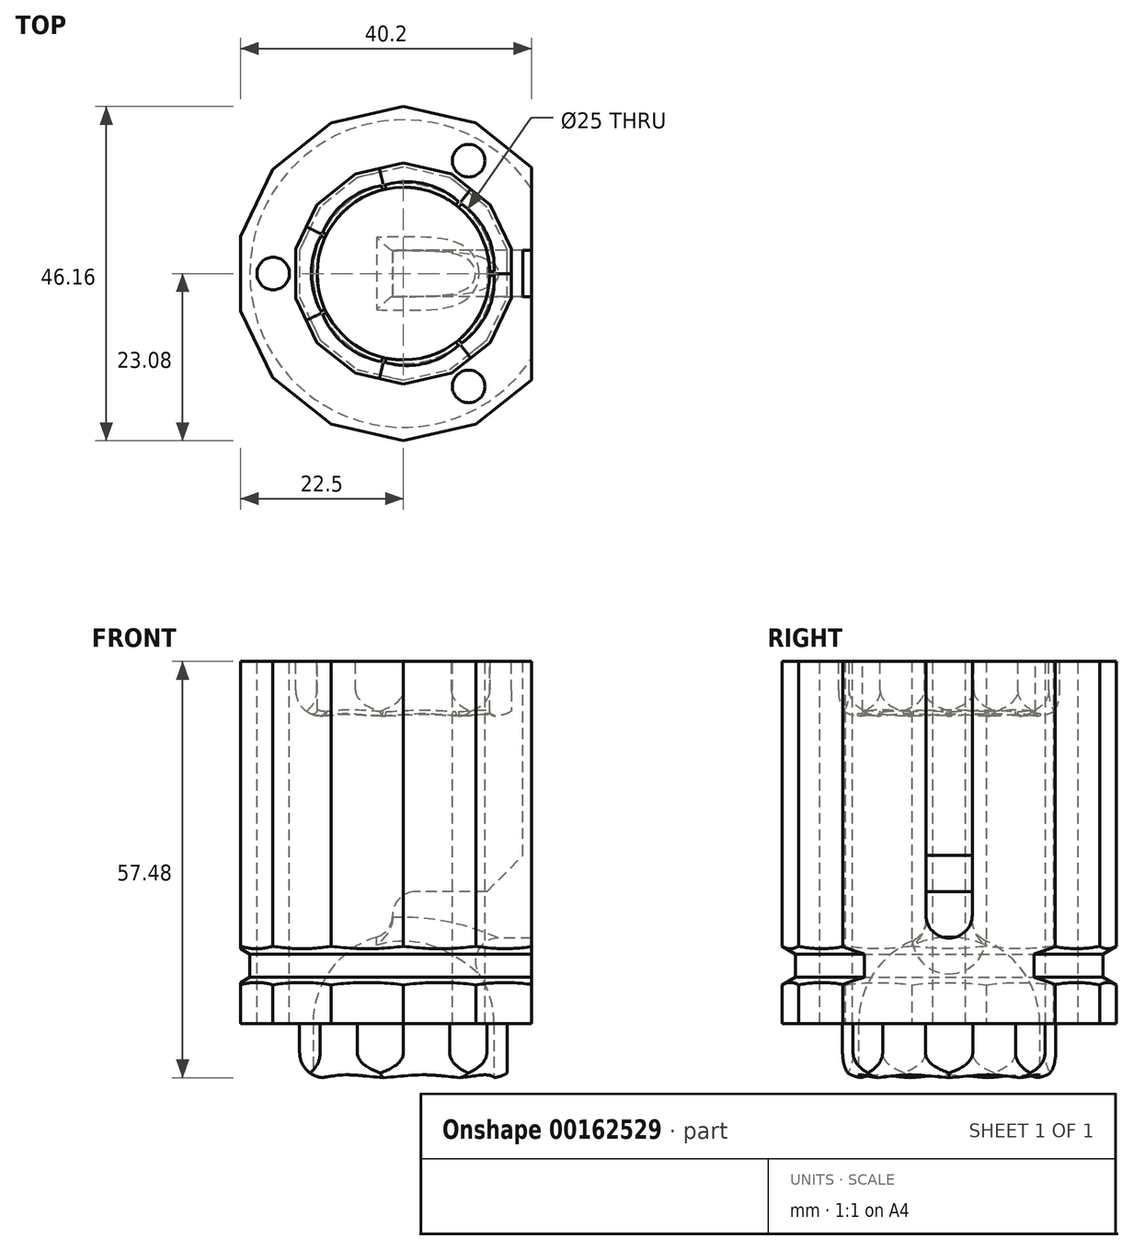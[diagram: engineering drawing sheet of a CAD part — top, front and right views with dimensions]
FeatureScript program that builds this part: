
annotation { "Feature Type Name" : "Feature", "Feature Type Description" : "" }
export const myFeature = defineFeature(function(context is Context, id is Id, definition is map)
    precondition{}
    {
        {
            var Q0;
            Q0=qCreatedBy(makeId("Top.planeOp"),FACE);
            var sketch = newSketch(context, id + "F0", { "sketchPlane" : qUnion([Q0])});
            skCircle(sketch, "E0", {"center": v(0, 0) * mm, "radius": 12.5 * mm});
            skCircle(sketch, "E1.cCircle", {"center": v(0, 0) * mm, "radius": 17.5 * mm, "construction": true});
            skLineSegment(sketch, "E1.0", {"start": v(17.5, 8.43) * mm, "end": v(17.5, -8.43) * mm, "construction": true});
            skLineSegment(sketch, "E1.1", {"start": v(17.5, -8.43) * mm, "end": v(4.32, -18.94) * mm, "construction": true});
            skLineSegment(sketch, "E1.2", {"start": v(4.32, -18.94) * mm, "end": v(-12.11, -15.19) * mm, "construction": true});
            skLineSegment(sketch, "E1.3", {"start": v(-12.11, -15.19) * mm, "end": v(-19.42, 0) * mm, "construction": true});
            skLineSegment(sketch, "E1.4", {"start": v(-19.42, 0) * mm, "end": v(-12.11, 15.19) * mm, "construction": true});
            skLineSegment(sketch, "E1.5", {"start": v(-12.11, 15.19) * mm, "end": v(4.32, 18.94) * mm, "construction": true});
            skLineSegment(sketch, "E1.6", {"start": v(4.32, 18.94) * mm, "end": v(17.5, 8.43) * mm, "construction": true});
            skPoint(sketch, "E1.0.midPoint", {"position": v(17.5, 0) * mm});
            skArc(sketch, "E2", {"start": v(7.16, 16.67) * mm, "mid": v(13.9, 17.43) * mm, "end": v(14.66, 10.69) * mm, "construction": true});
            skArc(sketch, "E3", {"start": v(0.79, 18.13) * mm, "mid": v(-4.96, 21.74) * mm, "end": v(-8.57, 16) * mm, "construction": true});
            skArc(sketch, "E4", {"start": v(-13.68, 11.92) * mm, "mid": v(-20.1, 9.68) * mm, "end": v(-17.85, 3.27) * mm, "construction": true});
            skArc(sketch, "E5", {"start": v(-17.85, -3.27) * mm, "mid": v(-20.1, -9.68) * mm, "end": v(-13.68, -11.92) * mm, "construction": true});
            skArc(sketch, "E6", {"start": v(-8.57, -16) * mm, "mid": v(-4.96, -21.74) * mm, "end": v(0.79, -18.13) * mm, "construction": true});
            skArc(sketch, "E7", {"start": v(14.66, -10.69) * mm, "mid": v(13.9, -17.43) * mm, "end": v(7.16, -16.67) * mm, "construction": true});
            skCircle(sketch, "E8.cCircle", {"center": v(0, 0) * mm, "radius": 22.5 * mm, "construction": true});
            skLineSegment(sketch, "E8.0", {"start": v(22.5, 5.14) * mm, "end": v(22.5, -5.14) * mm});
            skLineSegment(sketch, "E8.1", {"start": v(22.5, -5.14) * mm, "end": v(18.04, -14.39) * mm});
            skLineSegment(sketch, "E8.2", {"start": v(18.04, -14.39) * mm, "end": v(10.01, -20.8) * mm});
            skLineSegment(sketch, "E8.3", {"start": v(10.01, -20.8) * mm, "end": v(0, -23.08) * mm});
            skLineSegment(sketch, "E8.4", {"start": v(0, -23.08) * mm, "end": v(-10.01, -20.8) * mm});
            skLineSegment(sketch, "E8.5", {"start": v(-10.01, -20.8) * mm, "end": v(-18.04, -14.39) * mm});
            skLineSegment(sketch, "E8.6", {"start": v(-18.04, -14.39) * mm, "end": v(-22.5, -5.14) * mm});
            skLineSegment(sketch, "E8.7", {"start": v(-22.5, -5.14) * mm, "end": v(-22.5, 5.14) * mm});
            skLineSegment(sketch, "E8.8", {"start": v(-22.5, 5.14) * mm, "end": v(-18.04, 14.39) * mm});
            skLineSegment(sketch, "E8.9", {"start": v(-18.04, 14.39) * mm, "end": v(-10.01, 20.8) * mm});
            skLineSegment(sketch, "E8.10", {"start": v(-10.01, 20.8) * mm, "end": v(0, 23.08) * mm});
            skLineSegment(sketch, "E8.11", {"start": v(0, 23.08) * mm, "end": v(10.01, 20.8) * mm});
            skLineSegment(sketch, "E8.12", {"start": v(10.01, 20.8) * mm, "end": v(18.04, 14.39) * mm});
            skLineSegment(sketch, "E8.13", {"start": v(18.04, 14.39) * mm, "end": v(22.5, 5.14) * mm});
            skPoint(sketch, "E8.0.midPoint", {"position": v(22.5, 0) * mm});
            skSolve(sketch);
        }
        {
            var Q0;
            Q0=qSketchRegion(id+"F0",true);
            extrude(context, id + "F1", {"entities" : qUnion([Q0]), "endBound" : BoundingType.SYMMETRIC, "depth" : 50 * mm, "offsetDistance" : 25 * mm});
        }
        {
            var Q0;
            Q0=makeQuery(id+"F1.opExtrude","CAP_FACE",FACE,{"disambiguationData":[OSD([sQuery(id+"F0.wireOp",EDGE,"E0"),sQuery(id+"F0.wireOp",EDGE,"E1.0"),sQuery(id+"F0.wireOp",EDGE,"E1.1"),sQuery(id+"F0.wireOp",EDGE,"E1.2"),sQuery(id+"F0.wireOp",EDGE,"E1.3"),sQuery(id+"F0.wireOp",EDGE,"E1.4"),sQuery(id+"F0.wireOp",EDGE,"E1.5"),sQuery(id+"F0.wireOp",EDGE,"E1.6"),sQuery(id+"F0.wireOp",EDGE,"E2"),sQuery(id+"F0.wireOp",EDGE,"E3"),sQuery(id+"F0.wireOp",EDGE,"E4"),sQuery(id+"F0.wireOp",EDGE,"E5"),sQuery(id+"F0.wireOp",EDGE,"E6"),sQuery(id+"F0.wireOp",EDGE,"E7")])],"isStart":false});
            var sketch = newSketch(context, id + "F2", { "sketchPlane" : qUnion([Q0])});
            skLineSegment(sketch, "E9", {"start": v(0, 0) * mm, "end": v(11.38, 19.7) * mm, "construction": true});
            skCircle(sketch, "E10", {"center": v(9, 15.59) * mm, "radius": 2.25 * mm});
            skCircle(sketch, "E11.1.0", {"center": v(-18, 0) * mm, "radius": 2.25 * mm});
            skCircle(sketch, "E11.2.0", {"center": v(9, -15.59) * mm, "radius": 2.25 * mm});
            skPoint(sketch, "E11.center", {"position": v(0, 0) * mm});
            skSolve(sketch);
        }
        {
            var Q0;
            Q0=qSketchRegion(id+"F2",true);
            extrude(context, id + "F3", {"entities" : qUnion([Q0]), "operationType" : NewBodyOperationType.REMOVE, "oppositeDirection" : true, "depth" : 50 * mm, "offsetDistance" : 25 * mm});
        }
        {
            var Q0;
            Q0=makeQuery(id+"F1.opExtrude","CAP_FACE",FACE,{"disambiguationData":[OSD([sQuery(id+"F0.wireOp",EDGE,"E0"),sQuery(id+"F0.wireOp",EDGE,"E1.0"),sQuery(id+"F0.wireOp",EDGE,"E1.1"),sQuery(id+"F0.wireOp",EDGE,"E1.2"),sQuery(id+"F0.wireOp",EDGE,"E1.3"),sQuery(id+"F0.wireOp",EDGE,"E1.4"),sQuery(id+"F0.wireOp",EDGE,"E1.5"),sQuery(id+"F0.wireOp",EDGE,"E1.6"),sQuery(id+"F0.wireOp",EDGE,"E2"),sQuery(id+"F0.wireOp",EDGE,"E3"),sQuery(id+"F0.wireOp",EDGE,"E4"),sQuery(id+"F0.wireOp",EDGE,"E5"),sQuery(id+"F0.wireOp",EDGE,"E6"),sQuery(id+"F0.wireOp",EDGE,"E7")])],"isStart":false});
            var sketch = newSketch(context, id + "F4", { "sketchPlane" : qUnion([Q0])});
            skCircle(sketch, "E12", {"center": v(0, 0) * mm, "radius": 12.5 * mm});
            skCircle(sketch, "E13.cCircle", {"center": v(0, 0) * mm, "radius": 14.9 * mm, "construction": true});
            skLineSegment(sketch, "E13.0", {"start": v(14.9, 3.4) * mm, "end": v(14.9, -3.4) * mm});
            skLineSegment(sketch, "E13.1", {"start": v(14.9, -3.4) * mm, "end": v(11.95, -9.53) * mm});
            skLineSegment(sketch, "E13.2", {"start": v(11.95, -9.53) * mm, "end": v(6.63, -13.77) * mm});
            skLineSegment(sketch, "E13.3", {"start": v(6.63, -13.77) * mm, "end": v(0, -15.28) * mm});
            skLineSegment(sketch, "E13.4", {"start": v(0, -15.28) * mm, "end": v(-6.63, -13.77) * mm});
            skLineSegment(sketch, "E13.5", {"start": v(-6.63, -13.77) * mm, "end": v(-11.95, -9.53) * mm});
            skLineSegment(sketch, "E13.6", {"start": v(-11.95, -9.53) * mm, "end": v(-14.9, -3.4) * mm});
            skLineSegment(sketch, "E13.7", {"start": v(-14.9, -3.4) * mm, "end": v(-14.9, 3.4) * mm});
            skLineSegment(sketch, "E13.8", {"start": v(-14.9, 3.4) * mm, "end": v(-11.95, 9.53) * mm});
            skLineSegment(sketch, "E13.9", {"start": v(-11.95, 9.53) * mm, "end": v(-6.63, 13.77) * mm});
            skLineSegment(sketch, "E13.10", {"start": v(-6.63, 13.77) * mm, "end": v(0, 15.28) * mm});
            skLineSegment(sketch, "E13.11", {"start": v(0, 15.28) * mm, "end": v(6.63, 13.77) * mm});
            skLineSegment(sketch, "E13.12", {"start": v(6.63, 13.77) * mm, "end": v(11.95, 9.53) * mm});
            skLineSegment(sketch, "E13.13", {"start": v(11.95, 9.53) * mm, "end": v(14.9, 3.4) * mm});
            skPoint(sketch, "E13.0.midPoint", {"position": v(14.9, 0) * mm});
            skSolve(sketch);
        }
        {
            var Q0;
            Q0=qSketchRegion(id+"F4",true);
            extrude(context, id + "F5", {"entities" : qUnion([Q0]), "operationType" : NewBodyOperationType.REMOVE, "oppositeDirection" : true, "depth" : 7.5 * mm, "offsetDistance" : 25 * mm});
        }
        {
            var Q0;
            Q0=makeQuery(id+"F5.boolean.opBoolean","COPY",EDGE,{"derivedFrom":makeQuery(id+"F5.opExtrude","CAP_EDGE",EDGE,{"disambiguationData":[OSD([sQuery(id+"F4.wireOp",EDGE,"E13.9")])],"isStart":false})});
            var Q1;
            Q1=makeQuery(id+"F5.boolean.opBoolean","COPY",EDGE,{"derivedFrom":makeQuery(id+"F5.opExtrude","CAP_EDGE",EDGE,{"disambiguationData":[OSD([sQuery(id+"F4.wireOp",EDGE,"E13.11")])],"isStart":false})});
            var Q2;
            Q2=makeQuery(id+"F5.boolean.opBoolean","COPY",EDGE,{"derivedFrom":makeQuery(id+"F5.opExtrude","CAP_EDGE",EDGE,{"disambiguationData":[OSD([sQuery(id+"F4.wireOp",EDGE,"E13.13")])],"isStart":false})});
            var Q3;
            Q3=makeQuery(id+"F5.boolean.opBoolean","COPY",EDGE,{"derivedFrom":makeQuery(id+"F5.opExtrude","CAP_EDGE",EDGE,{"disambiguationData":[OSD([sQuery(id+"F4.wireOp",EDGE,"E13.1")])],"isStart":false})});
            var Q4;
            Q4=makeQuery(id+"F5.boolean.opBoolean","COPY",EDGE,{"derivedFrom":makeQuery(id+"F5.opExtrude","CAP_EDGE",EDGE,{"disambiguationData":[OSD([sQuery(id+"F4.wireOp",EDGE,"E13.3")])],"isStart":false})});
            var Q5;
            Q5=makeQuery(id+"F5.boolean.opBoolean","COPY",EDGE,{"derivedFrom":makeQuery(id+"F5.opExtrude","CAP_EDGE",EDGE,{"disambiguationData":[OSD([sQuery(id+"F4.wireOp",EDGE,"E13.5")])],"isStart":false})});
            var Q6;
            {var subQ0=sQuery(id+"F4.wireOp",EDGE,"E13.8");var subQ1=sQuery(id+"F4.wireOp",EDGE,"E13.7");Q6=makeQuery(id+"F5.boolean.opBoolean","COPY",EDGE,{"disambiguationData":[TD([makeQuery(id+"F5.opExtrude","SWEPT_FACE",FACE,{"disambiguationData":[OSD([subQ0])]})])],"derivedFrom":makeQuery(id+"F5.opExtrude","CAP_EDGE",EDGE,{"disambiguationData":[OSD([subQ1])],"isStart":false})});}
            fillet(context, id + "F6", {"entities" : qUnion([Q0, Q1, Q2, Q3, Q4, Q5, Q6]), "radius" : 3.5 * mm, "tangentPropagation" : true, "allowEdgeOverflow" : false});
        }
        {
            var Q0;
            Q0=makeQuery(id+"F1.opExtrude","CAP_FACE",FACE,{"disambiguationData":[OSD([sQuery(id+"F0.wireOp",EDGE,"E0"),sQuery(id+"F0.wireOp",EDGE,"E1.0"),sQuery(id+"F0.wireOp",EDGE,"E1.1"),sQuery(id+"F0.wireOp",EDGE,"E1.2"),sQuery(id+"F0.wireOp",EDGE,"E1.3"),sQuery(id+"F0.wireOp",EDGE,"E1.4"),sQuery(id+"F0.wireOp",EDGE,"E1.5"),sQuery(id+"F0.wireOp",EDGE,"E1.6"),sQuery(id+"F0.wireOp",EDGE,"E2"),sQuery(id+"F0.wireOp",EDGE,"E3"),sQuery(id+"F0.wireOp",EDGE,"E4"),sQuery(id+"F0.wireOp",EDGE,"E5"),sQuery(id+"F0.wireOp",EDGE,"E6"),sQuery(id+"F0.wireOp",EDGE,"E7")])],"isStart":true});
            var sketch = newSketch(context, id + "F7", { "sketchPlane" : qUnion([Q0])});
            skCircle(sketch, "E14", {"center": v(0, 0) * mm, "radius": 12.5 * mm});
            skCircle(sketch, "E15.cCircle", {"center": v(0, 0) * mm, "radius": 14.35 * mm, "construction": true});
            skLineSegment(sketch, "E15.0", {"start": v(14.35, 3.28) * mm, "end": v(14.35, -3.28) * mm});
            skLineSegment(sketch, "E15.1", {"start": v(14.35, -3.28) * mm, "end": v(11.5, -9.18) * mm});
            skLineSegment(sketch, "E15.2", {"start": v(11.5, -9.18) * mm, "end": v(6.39, -13.26) * mm});
            skLineSegment(sketch, "E15.3", {"start": v(6.39, -13.26) * mm, "end": v(0, -14.72) * mm});
            skLineSegment(sketch, "E15.4", {"start": v(0, -14.72) * mm, "end": v(-6.39, -13.26) * mm});
            skLineSegment(sketch, "E15.5", {"start": v(-6.39, -13.26) * mm, "end": v(-11.5, -9.18) * mm});
            skLineSegment(sketch, "E15.6", {"start": v(-11.5, -9.18) * mm, "end": v(-14.35, -3.28) * mm});
            skLineSegment(sketch, "E15.7", {"start": v(-14.35, -3.28) * mm, "end": v(-14.35, 3.28) * mm});
            skLineSegment(sketch, "E15.8", {"start": v(-14.35, 3.28) * mm, "end": v(-11.5, 9.18) * mm});
            skLineSegment(sketch, "E15.9", {"start": v(-11.5, 9.18) * mm, "end": v(-6.39, 13.26) * mm});
            skLineSegment(sketch, "E15.10", {"start": v(-6.39, 13.26) * mm, "end": v(0, 14.72) * mm});
            skLineSegment(sketch, "E15.11", {"start": v(0, 14.72) * mm, "end": v(6.39, 13.26) * mm});
            skLineSegment(sketch, "E15.12", {"start": v(6.39, 13.26) * mm, "end": v(11.5, 9.18) * mm});
            skLineSegment(sketch, "E15.13", {"start": v(11.5, 9.18) * mm, "end": v(14.35, 3.28) * mm});
            skPoint(sketch, "E15.0.midPoint", {"position": v(14.35, 0) * mm});
            skSolve(sketch);
        }
        {
            var Q0;
            Q0=qSketchRegion(id+"F7",true);
            extrude(context, id + "F8", {"entities" : qUnion([Q0]), "operationType" : NewBodyOperationType.ADD, "depth" : 7.5 * mm, "offsetDistance" : 25 * mm});
        }
        {
            var Q0;
            Q0=makeQuery(id+"F8.opExtrude","CAP_EDGE",EDGE,{"disambiguationData":[OSD([sQuery(id+"F7.wireOp",EDGE,"E15.1")])],"isStart":false});
            var Q1;
            Q1=makeQuery(id+"F8.opExtrude","CAP_EDGE",EDGE,{"disambiguationData":[OSD([sQuery(id+"F7.wireOp",EDGE,"E15.3")])],"isStart":false});
            var Q2;
            Q2=makeQuery(id+"F8.opExtrude","CAP_EDGE",EDGE,{"disambiguationData":[OSD([sQuery(id+"F7.wireOp",EDGE,"E15.5")])],"isStart":false});
            var Q3;
            Q3=makeQuery(id+"F8.opExtrude","CAP_EDGE",EDGE,{"disambiguationData":[OSD([sQuery(id+"F7.wireOp",EDGE,"E15.7")])],"isStart":false});
            var Q4;
            Q4=makeQuery(id+"F8.opExtrude","CAP_EDGE",EDGE,{"disambiguationData":[OSD([sQuery(id+"F7.wireOp",EDGE,"E15.9")])],"isStart":false});
            var Q5;
            Q5=makeQuery(id+"F8.opExtrude","CAP_EDGE",EDGE,{"disambiguationData":[OSD([sQuery(id+"F7.wireOp",EDGE,"E15.11")])],"isStart":false});
            var Q6;
            Q6=makeQuery(id+"F8.opExtrude","CAP_EDGE",EDGE,{"disambiguationData":[OSD([sQuery(id+"F7.wireOp",EDGE,"E15.13")])],"isStart":false});
            fillet(context, id + "F9", {"entities" : qUnion([Q0, Q1, Q2, Q3, Q4, Q5, Q6]), "radius" : 3.5 * mm, "tangentPropagation" : true, "allowEdgeOverflow" : false});
        }
        {
            var Q0;
            Q0=makeQuery(id+"F1.opExtrude","CAP_FACE",FACE,{"disambiguationData":[OSD([sQuery(id+"F0.wireOp",EDGE,"E0"),sQuery(id+"F0.wireOp",EDGE,"E1.0"),sQuery(id+"F0.wireOp",EDGE,"E1.1"),sQuery(id+"F0.wireOp",EDGE,"E1.2"),sQuery(id+"F0.wireOp",EDGE,"E1.3"),sQuery(id+"F0.wireOp",EDGE,"E1.4"),sQuery(id+"F0.wireOp",EDGE,"E1.5"),sQuery(id+"F0.wireOp",EDGE,"E1.6"),sQuery(id+"F0.wireOp",EDGE,"E2"),sQuery(id+"F0.wireOp",EDGE,"E3"),sQuery(id+"F0.wireOp",EDGE,"E4"),sQuery(id+"F0.wireOp",EDGE,"E5"),sQuery(id+"F0.wireOp",EDGE,"E6"),sQuery(id+"F0.wireOp",EDGE,"E7")])],"isStart":true});
            var sketch = newSketch(context, id + "F10", { "sketchPlane" : qUnion([Q0])});
            skLineSegment(sketch, "E16.bottom", {"start": v(22.5, -14.66) * mm, "end": v(17.7, -14.66) * mm});
            skLineSegment(sketch, "E16.top", {"start": v(22.5, 14.66) * mm, "end": v(17.7, 14.66) * mm});
            skLineSegment(sketch, "E16.left", {"start": v(22.5, -14.66) * mm, "end": v(22.5, 14.66) * mm});
            skLineSegment(sketch, "E16.right", {"start": v(17.7, -14.66) * mm, "end": v(17.7, 14.66) * mm});
            skPoint(sketch, "E16.middle", {"position": v(20.1, 0) * mm});
            skSolve(sketch);
        }
        {
            var Q0;
            Q0=qSketchRegion(id+"F10",true);
            extrude(context, id + "F11", {"entities" : qUnion([Q0]), "operationType" : NewBodyOperationType.REMOVE, "endBound" : BoundingType.THROUGH_ALL, "oppositeDirection" : true, "depth" : 15 * mm, "offsetDistance" : 25 * mm});
        }
        {
            var Q0;
            Q0=makeQuery(id+"F1.opExtrude","CAP_FACE",FACE,{"disambiguationData":[OSD([sQuery(id+"F0.wireOp",EDGE,"E0"),sQuery(id+"F0.wireOp",EDGE,"E1.0"),sQuery(id+"F0.wireOp",EDGE,"E1.1"),sQuery(id+"F0.wireOp",EDGE,"E1.2"),sQuery(id+"F0.wireOp",EDGE,"E1.3"),sQuery(id+"F0.wireOp",EDGE,"E1.4"),sQuery(id+"F0.wireOp",EDGE,"E1.5"),sQuery(id+"F0.wireOp",EDGE,"E1.6"),sQuery(id+"F0.wireOp",EDGE,"E2"),sQuery(id+"F0.wireOp",EDGE,"E3"),sQuery(id+"F0.wireOp",EDGE,"E4"),sQuery(id+"F0.wireOp",EDGE,"E5"),sQuery(id+"F0.wireOp",EDGE,"E6"),sQuery(id+"F0.wireOp",EDGE,"E7")])],"isStart":false});
            var sketch = newSketch(context, id + "F12", { "sketchPlane" : qUnion([Q0])});
            skLineSegment(sketch, "E17.bottom", {"start": v(18.9, -3.2) * mm, "end": v(16.5, -3.2) * mm});
            skLineSegment(sketch, "E17.top", {"start": v(18.9, 3.2) * mm, "end": v(16.5, 3.2) * mm});
            skLineSegment(sketch, "E17.left", {"start": v(18.9, -3.2) * mm, "end": v(18.9, 3.2) * mm});
            skLineSegment(sketch, "E17.right", {"start": v(16.5, -3.2) * mm, "end": v(16.5, 3.2) * mm});
            skPoint(sketch, "E17.middle", {"position": v(17.7, 0) * mm});
            skSolve(sketch);
        }
        {
            var Q0;
            Q0=qSketchRegion(id+"F12",true);
            extrude(context, id + "F13", {"entities" : qUnion([Q0]), "operationType" : NewBodyOperationType.REMOVE, "oppositeDirection" : true, "depth" : 35 * mm, "offsetDistance" : 25 * mm});
        }
        {
            var Q0;
            Q0=qCreatedBy(makeId("Top.planeOp"),FACE);
            var sketch = newSketch(context, id + "F14", { "sketchPlane" : qUnion([Q0])});
            skCircle(sketch, "E18", {"center": v(0, 0) * mm, "radius": 12.5 * mm});
            skSolve(sketch);
        }
        {
            var Q0;
            Q0=qSketchRegion(id+"F14",true);
            extrude(context, id + "F15", {"entities" : qUnion([Q0]), "operationType" : NewBodyOperationType.ADD, "endBound" : BoundingType.SYMMETRIC, "depth" : 50 * mm, "offsetDistance" : 25 * mm});
        }
        {
            var Q0;
            Q0=makeQuery(id+"F15.boolean.opBoolean","MERGE",FACE,{"derivedFrom":[makeQuery(id+"F1.opExtrude","CAP_FACE",FACE,{"disambiguationData":[OSD([sQuery(id+"F0.wireOp",EDGE,"E0"),sQuery(id+"F0.wireOp",EDGE,"E1.0"),sQuery(id+"F0.wireOp",EDGE,"E1.1"),sQuery(id+"F0.wireOp",EDGE,"E1.2"),sQuery(id+"F0.wireOp",EDGE,"E1.3"),sQuery(id+"F0.wireOp",EDGE,"E1.4"),sQuery(id+"F0.wireOp",EDGE,"E1.5"),sQuery(id+"F0.wireOp",EDGE,"E1.6"),sQuery(id+"F0.wireOp",EDGE,"E2"),sQuery(id+"F0.wireOp",EDGE,"E3"),sQuery(id+"F0.wireOp",EDGE,"E4"),sQuery(id+"F0.wireOp",EDGE,"E5"),sQuery(id+"F0.wireOp",EDGE,"E6"),sQuery(id+"F0.wireOp",EDGE,"E7")])],"isStart":true}),makeQuery(id+"F15.opExtrude","CAP_FACE",FACE,{"disambiguationData":[OSD([sQuery(id+"F14.wireOp",EDGE,"E18")])],"isStart":true})]});
            var sketch = newSketch(context, id + "F16", { "sketchPlane" : qUnion([Q0])});
            skArc(sketch, "E19", {"start": v(0, 12.5) * mm, "mid": v(-12.5, 0) * mm, "end": v(0, -12.5) * mm});
            skLineSegment(sketch, "E20", {"start": v(0, 12.5) * mm, "end": v(0, -12.5) * mm});
            skSolve(sketch);
        }
        {
            var Q0;
            Q0=qSketchRegion(id+"F16",true);
            var Q1;
            Q1=sQuery(id+"F16.wireOp",EDGE,"E20");
            revolve(context, id + "F17", {"operationType" : NewBodyOperationType.REMOVE, "entities" : qUnion([Q0]), "axis" : qUnion([Q1]), "revolveType" : RevolveType.FULL, "oppositeDirection" : true});
        }
        {
            var Q0;
            Q0=qCreatedBy(makeId("Front.planeOp"),FACE);
            var sketch = newSketch(context, id + "F18", { "sketchPlane" : qUnion([Q0])});
            skLineSegment(sketch, "E21.bottom", {"start": v(16.5, -3.2) * mm, "end": v(-1.5, -3.2) * mm, "construction": true});
            skLineSegment(sketch, "E21.top", {"start": v(16.5, 3.2) * mm, "end": v(-1.5, 3.2) * mm, "construction": true});
            skLineSegment(sketch, "E21.left", {"start": v(16.5, -3.2) * mm, "end": v(16.5, 3.2) * mm, "construction": true});
            skLineSegment(sketch, "E21.right", {"start": v(-1.5, -3.2) * mm, "end": v(-1.5, 3.2) * mm, "construction": true});
            skPoint(sketch, "E21.middle", {"position": v(7.5, 0) * mm});
            skLineSegment(sketch, "E22", {"start": v(-5.3, -5) * mm, "end": v(17.52, -5) * mm, "construction": true});
            skLineSegment(sketch, "E23.MirrorCS", {"start": v(16.5, -6.8) * mm, "end": v(-1.5, -6.8) * mm});
            skLineSegment(sketch, "E24.MirrorCS", {"start": v(16.5, -6.8) * mm, "end": v(16.5, -13.2) * mm, "construction": true});
            skLineSegment(sketch, "E25.MirrorCS", {"start": v(16.5, -13.2) * mm, "end": v(-1.5, -13.2) * mm});
            skPoint(sketch, "E26.MirrorP", {"position": v(7.5, -10) * mm});
            skLineSegment(sketch, "E27.MirrorCS", {"start": v(-1.5, -6.8) * mm, "end": v(-1.5, -13.2) * mm});
            skLineSegment(sketch, "E28", {"start": v(16.5, -6.8) * mm, "end": v(17.7, -6.8) * mm});
            skLineSegment(sketch, "E29", {"start": v(17.7, -6.8) * mm, "end": v(17.7, -13.2) * mm});
            skLineSegment(sketch, "E30", {"start": v(17.7, -13.2) * mm, "end": v(16.5, -13.2) * mm});
            skSolve(sketch);
        }
        {
            var Q0;
            Q0=qSketchRegion(id+"F18",true);
            extrude(context, id + "F19", {"entities" : qUnion([Q0]), "operationType" : NewBodyOperationType.REMOVE, "endBound" : BoundingType.SYMMETRIC, "oppositeDirection" : true, "depth" : 6.4 * mm, "offsetDistance" : 25 * mm});
        }
        {
            var Q0;
            Q0=makeQuery(id+"F19.boolean.opBoolean","COPY",EDGE,{"derivedFrom":makeQuery(id+"F19.opExtrude","CAP_EDGE",EDGE,{"disambiguationData":[OSD([sQuery(id+"F18.wireOp",EDGE,"E25.MirrorCS"),sQuery(id+"F18.wireOp",EDGE,"E30")])],"isStart":false})});
            var Q1;
            Q1=makeQuery(id+"F19.boolean.opBoolean","COPY",EDGE,{"derivedFrom":makeQuery(id+"F19.opExtrude","CAP_EDGE",EDGE,{"disambiguationData":[OSD([sQuery(id+"F18.wireOp",EDGE,"E25.MirrorCS"),sQuery(id+"F18.wireOp",EDGE,"E30")])],"isStart":true})});
            fillet(context, id + "F20", {"entities" : qUnion([Q0, Q1]), "radius" : 3.2 * mm, "tangentPropagation" : true, "allowEdgeOverflow" : false});
        }
        {
            var Q0;
            Q0=makeQuery(id+"F19.boolean.opBoolean","INTERSECT",EDGE,{"derivedFrom":[makeQuery(id+"F13.boolean.opBoolean","COPY",FACE,{"derivedFrom":makeQuery(id+"F13.opExtrude","SWEPT_FACE",FACE,{"disambiguationData":[OSD([sQuery(id+"F12.wireOp",EDGE,"E17.right")])]})}),makeQuery(id+"F19.opExtrude","SWEPT_FACE",FACE,{"disambiguationData":[OSD([sQuery(id+"F18.wireOp",EDGE,"E23.MirrorCS"),sQuery(id+"F18.wireOp",EDGE,"E28")])]})]});
            chamfer(context, id + "F21", {"entities" : qUnion([Q0]), "width" : 5 * mm, "tangentPropagation" : true});
        }
        {
            var Q0;
            Q0=makeQuery(id+"F19.boolean.opBoolean","COPY",EDGE,{"derivedFrom":makeQuery(id+"F19.opExtrude","SWEPT_EDGE",EDGE,{"disambiguationData":[OSD([sQuery(id+"F18.wireOp",EDGE,"E23.MirrorCS"),sQuery(id+"F18.wireOp",EDGE,"E27.MirrorCS")])]})});
            var Q1;
            Q1=makeQuery(id+"F20.opFillet","BLEND_EDGE",EDGE,{"blendedFrom":[makeQuery(id+"F19.boolean.opBoolean","COPY",EDGE,{"derivedFrom":makeQuery(id+"F19.opExtrude","CAP_EDGE",EDGE,{"disambiguationData":[OSD([sQuery(id+"F18.wireOp",EDGE,"E25.MirrorCS"),sQuery(id+"F18.wireOp",EDGE,"E30")])],"isStart":true})}),makeQuery(id+"F17.boolean.opBoolean","COPY",FACE,{"derivedFrom":makeQuery(id+"F17.opRevolve","SWEPT_FACE",FACE,{"disambiguationData":[OSD([sQuery(id+"F16.wireOp",EDGE,"E19")])]})})],"blendedInto":[makeQuery(id+"F17.boolean.opBoolean","COPY",FACE,{"derivedFrom":makeQuery(id+"F17.opRevolve","SWEPT_FACE",FACE,{"disambiguationData":[OSD([sQuery(id+"F16.wireOp",EDGE,"E19")])]})})]});
            var Q2;
            Q2=makeQuery(id+"F19.boolean.opBoolean","INTERSECT",EDGE,{"derivedFrom":[makeQuery(id+"F17.boolean.opBoolean","COPY",FACE,{"derivedFrom":makeQuery(id+"F17.opRevolve","SWEPT_FACE",FACE,{"disambiguationData":[OSD([sQuery(id+"F16.wireOp",EDGE,"E19")])]})}),makeQuery(id+"F19.opExtrude","SWEPT_FACE",FACE,{"disambiguationData":[OSD([sQuery(id+"F18.wireOp",EDGE,"E27.MirrorCS")])]})]});
            fillet(context, id + "F22", {"entities" : qUnion([Q0, Q1, Q2]), "radius" : 3.2 * mm, "tangentPropagation" : true, "allowEdgeOverflow" : false});
        }
        {
            var Q0;
            Q0=qCreatedBy(makeId("Front.planeOp"),FACE);
            var sketch = newSketch(context, id + "F23", { "sketchPlane" : qUnion([Q0])});
            skLineSegment(sketch, "E31", {"start": v(0, 13.6) * mm, "end": v(0, 0) * mm, "construction": true});
            skCircle(sketch, "E32.cCircle", {"center": v(24, -17) * mm, "radius": 2.77 * mm, "construction": true});
            skLineSegment(sketch, "E32.0", {"start": v(26.77, -15.4) * mm, "end": v(26.77, -18.6) * mm});
            skLineSegment(sketch, "E32.1", {"start": v(26.77, -18.6) * mm, "end": v(24, -20.2) * mm});
            skLineSegment(sketch, "E32.2", {"start": v(24, -20.2) * mm, "end": v(21.23, -18.6) * mm});
            skLineSegment(sketch, "E32.3", {"start": v(21.23, -18.6) * mm, "end": v(21.23, -15.4) * mm});
            skLineSegment(sketch, "E32.4", {"start": v(21.23, -15.4) * mm, "end": v(24, -13.8) * mm});
            skLineSegment(sketch, "E32.5", {"start": v(24, -13.8) * mm, "end": v(26.77, -15.4) * mm});
            skPoint(sketch, "E32.0.midPoint", {"position": v(26.77, -17) * mm});
            skSolve(sketch);
        }
        {
            var Q0;
            Q0=qSketchRegion(id+"F23",true);
            var Q1;
            Q1=sQuery(id+"F23.wireOp",EDGE,"E31");
            revolve(context, id + "F24", {"operationType" : NewBodyOperationType.REMOVE, "entities" : qUnion([Q0]), "axis" : qUnion([Q1]), "revolveType" : RevolveType.FULL, "oppositeDirection" : true});
        }
        {
            var Q0;
            Q0=makeQuery(id+"F15.opExtrude","CAP_FACE",FACE,{"disambiguationData":[OSD([sQuery(id+"F14.wireOp",EDGE,"E18")])],"isStart":false});
            var sketch = newSketch(context, id + "F25", { "sketchPlane" : qUnion([Q0])});
            skCircle(sketch, "E33", {"center": v(0, 0) * mm, "radius": 12.5 * mm});
            skCircle(sketch, "E34", {"center": v(0, 0) * mm, "radius": 11.93 * mm});
            skSolve(sketch);
        }
        {
            var Q0;
            Q0 = qSketchRegion(id + "F25", true);
            var Q1;
            Q1=sQuery(id+"F25.wireOp",EDGE,"E33");
            extrude(context, id + "F26", {"entities" : qUnion([Q0]), "operationType" : NewBodyOperationType.REMOVE, "surfaceEntities" : qUnion([Q1]), "oppositeDirection" : true, "depth" : 7.5 * mm, "offsetDistance" : 25 * mm});
        }
        {
            var Q0;
            Q0=makeQuery(id+"F26.boolean.opBoolean","COPY",EDGE,{"derivedFrom":makeQuery(id+"F26.opExtrude","CAP_EDGE",EDGE,{"disambiguationData":[OSD([sQuery(id+"F25.wireOp",EDGE,"E34")])],"isStart":false})});
            fillet(context, id + "F27", {"entities" : qUnion([Q0]), "radius" : .6 * mm, "tangentPropagation" : true, "allowEdgeOverflow" : false});
        }
    });
